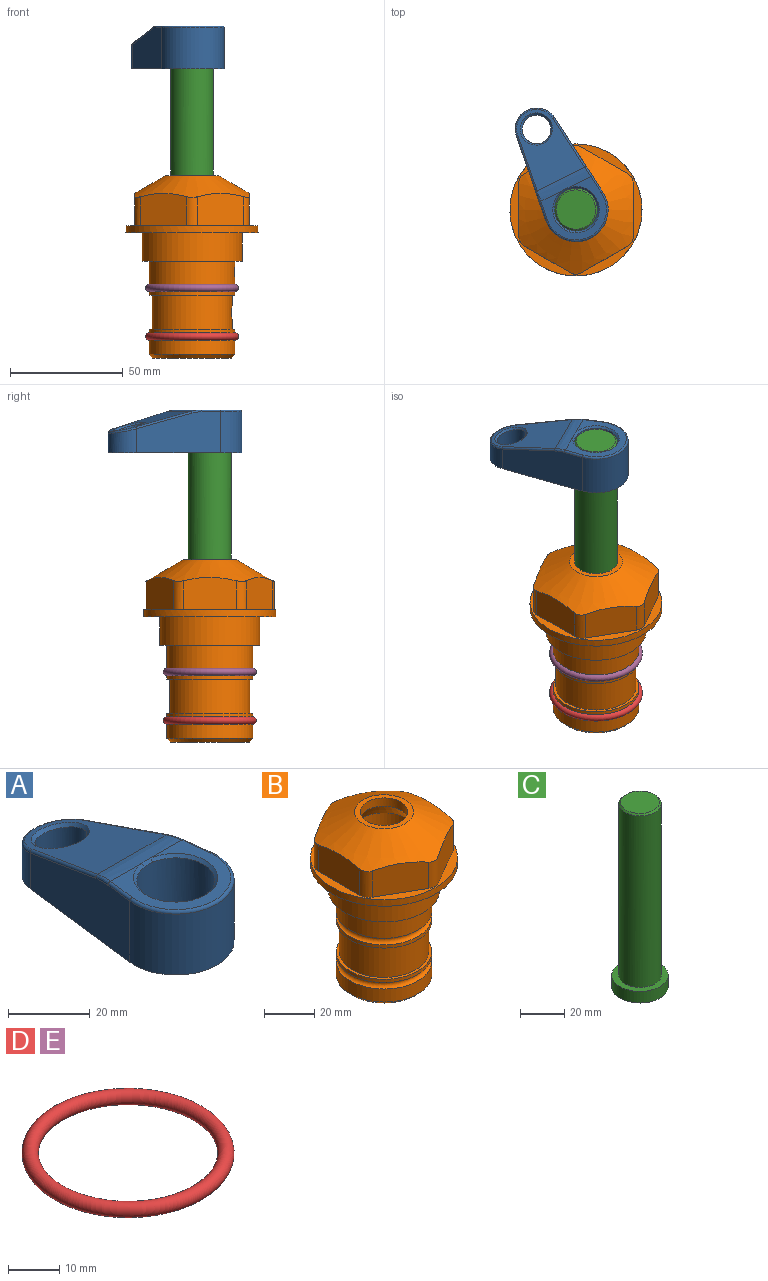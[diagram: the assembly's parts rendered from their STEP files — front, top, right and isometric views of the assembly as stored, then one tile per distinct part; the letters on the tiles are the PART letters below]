
ASSEMBLY  parts=5 mates=4
PART A: 31 faces, bbox 31.7x65.5x19.8 mm
  f0: plane 39.12x18.26mm, normal (0.99,0.12,0), area 612.2mm2, adj f1,f4,f7,f11,f13,f15
  f1: cylinder r=9.53mm len=18.91mm, axis (0,0,-1), area 296.1mm2, adj f0,f2,f7,f17
  f2: plane 39.12x18.26mm, normal (-0.99,0.12,0), area 612.2mm2, adj f1,f4,f7,f12,f14,f16
  f3: cylinder r=6.35mm len=12.7mm, axis (0,0,-1), area 362.4mm2, adj f7,f18
  f4: cylinder r=14.29mm len=28.58mm, axis (0,0,-1), area 882.2mm2, adj f0,f2,f7,f10
  f5: cylinder r=9.53mm len=19.05mm, axis (0,0,-1), area 1092.6mm2, adj f7,f19,f20
  f6: plane 26.99x23.69mm, normal (0,0,1), area 216.2mm2, adj f9,f10,f11,f12,f19
  f7: plane 63.5x28.58mm, normal (0,0,-1), area 661.8mm2, adj f0,f1,f2,f3,f4,f5,f22,f23
  f8: plane 33.52x23.6mm, normal (0,0.26,0.97), area 486mm2, adj f9,f15,f16,f17,f18
  f9: cylinder r=19.05mm len=24.72mm, axis (1,0,0), area 120.4mm2, adj f6,f8,f13,f14,f20
  f10: torus R=13.49mm, axis (0,0,1), area 59mm2, adj f4,f6,f11,f12
  f11: cylinder r=0.79mm len=8.67mm, axis (0.12,-0.99,0), area 10.8mm2, adj f0,f6,f10,f13
  f12: cylinder r=0.79mm len=8.67mm, axis (0.12,0.99,0), area 10.8mm2, adj f2,f6,f10,f14
  f13: bspline ~4.95x1.42mm, area 6.1mm2, adj f0,f9,f11,f15
  f14: bspline ~4.95x1.42mm, area 6.1mm2, adj f2,f9,f12,f16
  f15: cylinder r=0.79mm len=25.95mm, axis (0.12,-0.96,0.26), area 32.9mm2, adj f0,f8,f13,f17
  f16: cylinder r=0.79mm len=25.95mm, axis (0.12,0.96,-0.26), area 32.9mm2, adj f2,f8,f14,f17
  f17: bspline ~18.91x8.38mm, area 30mm2, adj f1,f8,f15,f16
  f18: bspline ~14.29x14.29mm, area 48.3mm2, adj f3,f8
  f19: cone r=9.53mm half-angle=45deg, axis (0,0,1), area 66.5mm2, adj f5,f6,f20
  f20: bspline ~3.22x0.96mm, area 3.5mm2, adj f5,f9,f19
  f21: plane 2.75x2.72mm, normal (0,0,-1), area 2.9mm2, adj f23,f25,f28
  f22: plane 23.05x15.88mm, normal (-0.99,-0.12,0), area 323.6mm2, adj f7,f25,f26,f27,f28,f29
  f23: plane 23.05x15.88mm, normal (0.99,-0.12,0), area 323.6mm2, adj f7,f21,f25,f27,f28,f30
  f24: cylinder r=9.53mm len=10.69mm, axis (0,0,-1), area 114.7mm2, adj f7,f27,f29,f30
  f25: cylinder r=12.7mm len=20.59mm, axis (0,0,-1), area 381.1mm2, adj f7,f21,f22,f23,f26,f28
  f26: plane 2.75x2.72mm, normal (0,0,-1), area 2.9mm2, adj f22,f25,f28
  f27: plane 19.72x18.37mm, normal (0,-0.26,-0.97), area 291.8mm2, adj f22,f23,f24,f28,f29,f30
  f28: cylinder r=15.88mm len=19.92mm, axis (1,0,0), area 54.8mm2, adj f21,f22,f23,f25,f26,f27
  f29: cylinder r=1.59mm len=11mm, axis (0,0,-1), area 34.7mm2, adj f7,f22,f24,f27
  f30: cylinder r=1.59mm len=11mm, axis (0,0,-1), area 34.7mm2, adj f7,f23,f24,f27
PART B: 36 faces, bbox 58.7x58.7x81 mm
  f0: cylinder r=17.78mm len=35.56mm, axis (0,0,1), area 1670.8mm2, adj f23,f24,f31
  f1: cylinder r=19.05mm len=38.1mm, axis (0,0,1), area 1191.9mm2, adj f26,f27,f30
  f2: plane 58.66x58.66mm, normal (0,0,-1), area 1150.6mm2, adj f3,f28
  f3: cylinder r=29.33mm len=58.66mm, axis (0,0,-1), area 585.1mm2, adj f2,f4
  f4: plane 58.66x58.66mm, normal (0,0,1), area 475.9mm2, adj f3,f5,f6,f7,f8,f9,f10,f11
  f5: plane 20.32x14.34mm, normal (-0.5,0.87,0), area 324.4mm2, adj f4,f15,f16,f17
  f6: plane 20.32x14.34mm, normal (0.5,0.87,0), area 324.4mm2, adj f4,f14,f15,f17
  f7: plane 23.48x14.34mm, normal (1,0,0), area 324.4mm2, adj f4,f13,f14,f17
  f8: plane 20.32x14.34mm, normal (0.5,-0.87,0), area 324.4mm2, adj f4,f12,f13,f17
  f9: plane 20.32x14.34mm, normal (-0.5,-0.87,0), area 324.4mm2, adj f4,f11,f12,f17
  f10: plane 23.48x14.34mm, normal (-1,0,0), area 324.4mm2, adj f4,f11,f16,f17
  f11: cylinder r=5.08mm len=12.85mm, axis (0,0,-1), area 67.2mm2, adj f4,f9,f10,f17
  f12: cylinder r=5.08mm len=12.85mm, axis (0,0,-1), area 67.2mm2, adj f4,f8,f9,f17
  f13: cylinder r=5.08mm len=12.85mm, axis (0,0,-1), area 67.2mm2, adj f4,f7,f8,f17
  f14: cylinder r=5.08mm len=12.85mm, axis (0,0,-1), area 67.2mm2, adj f4,f6,f7,f17
  f15: cylinder r=5.08mm len=12.85mm, axis (0,0,-1), area 67.2mm2, adj f4,f5,f6,f17
  f16: cylinder r=5.08mm len=12.85mm, axis (0,0,-1), area 67.2mm2, adj f4,f5,f10,f17
  f17: cone r=11.73mm half-angle=60deg, axis (0,0,-1), area 2071.8mm2, adj f5,f6,f7,f8,f9,f10,f11,f12
  f18: plane 23.46x23.46mm, normal (0,0,1), area 147.4mm2, adj f17,f35
  f19: plane 34.93x34.93mm, normal (0,0,-1), area 958mm2, adj f29
  f20: cylinder r=19.05mm len=38.1mm, axis (0,0,1), area 760.1mm2, adj f21,f29
  f21: torus R=19.05mm, axis (0,0,1), area 565.3mm2, adj f20,f22
  f22: cylinder r=19.05mm len=38.1mm, axis (0,0,1), area 190mm2, adj f21,f23
  f23: plane 38.1x38.1mm, normal (0,0,1), area 146.9mm2, adj f0,f22
  f24: plane 38.1x38.1mm, normal (0,0,-1), area 146.9mm2, adj f0,f25
  f25: cylinder r=19.05mm len=38.1mm, axis (0,0,1), area 190mm2, adj f24,f26
  f26: torus R=19.05mm, axis (0,0,1), area 565.3mm2, adj f1,f25
  f27: plane 44.45x44.45mm, normal (0,0,-1), area 411.7mm2, adj f1,f28
  f28: cylinder r=22.23mm len=44.45mm, axis (0,0,1), area 1773.5mm2, adj f2,f27
  f29: cone r=19.05mm half-angle=45deg, axis (0,0,1), area 257.5mm2, adj f19,f20
  f30: cylinder r=3.17mm len=6.75mm, axis (-1,0,0), area 128mm2, adj f1,f33
  f31: cylinder r=3.17mm len=6.35mm, axis (-1,0,0), area 102.5mm2, adj f0,f33
  f32: plane 25.4x25.4mm, normal (0,0,1), area 506.7mm2, adj f33
  f33: cylinder r=12.7mm len=66.42mm, axis (0,0,-1), area 5236.2mm2, adj f30,f31,f32,f34
  f34: cone r=9.53mm half-angle=30deg, axis (0,0,-1), area 443.4mm2, adj f33,f35
  f35: cylinder r=9.53mm len=19.05mm, axis (0,0,-1), area 240.9mm2, adj f18,f34
PART C: 6 faces, bbox 25.4x25.4x101.6 mm
  f0: plane 17.46x17.46mm, normal (0,0,1), area 239.5mm2, adj f5
  f1: plane 25.4x25.4mm, normal (0,0,-1), area 506.7mm2, adj f2
  f2: cylinder r=12.7mm len=25.4mm, axis (0,0,1), area 506.7mm2, adj f1,f3
  f3: plane 25.4x25.4mm, normal (0,0,1), area 221.7mm2, adj f2,f4
  f4: cylinder r=9.53mm len=94.46mm, axis (0,0,1), area 5653mm2, adj f3,f5
  f5: cone r=8.73mm half-angle=45deg, axis (0,0,-1), area 64.4mm2, adj f0,f4
PART D: 1 faces, bbox 44.7x44.7x3.2 mm
  f0: torus R=19.05mm, axis (0,0,1), area 1193.9mm2
PART E: same geometry as D
PLACE A rot(axis=(0,0,1),26.1deg) t=(0,0,28.35)mm
PLACE B at identity fixed
PLACE C rot(axis=(0,0,1),26.1deg) t=(0,0,27.55)mm
PLACE D t=(0,0,-21.59)mm
PLACE E at identity
MATE cylindrical B.f0 <-> C.f2  axis (0,0,1) through (0,0,-50.55)mm
MATE fastened B.f0 <-> D.f0  axis (0,0,1) through (0,0,-46.1)mm
MATE fastened B.f0 <-> E.f0  axis (0,0,1) through (0,0,-24.51)mm
MATE fastened C.f2 <-> A.f4  axis (0,0,1) through (0,0,91.05)mm
